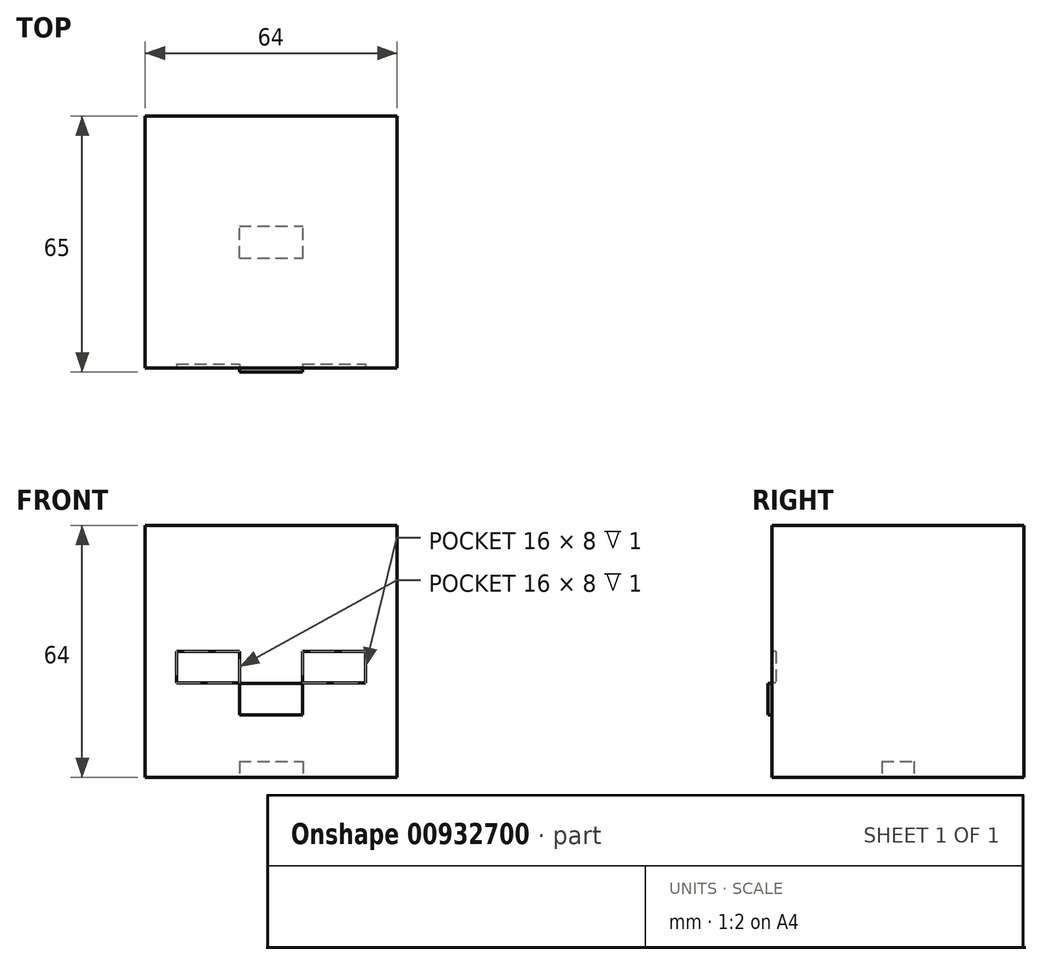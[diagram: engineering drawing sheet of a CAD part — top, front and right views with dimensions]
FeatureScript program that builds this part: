
annotation { "Feature Type Name" : "Feature", "Feature Type Description" : "" }
export const myFeature = defineFeature(function(context is Context, id is Id, definition is map)
    precondition{}
    {
        {
            var Q0;
            Q0=qCreatedBy(makeId("Top.planeOp"),FACE);
            var sketch = newSketch(context, id + "F0", { "sketchPlane" : qUnion([Q0])});
            skLineSegment(sketch, "E0.bottom", {"start": v(-32, 32) * mm, "end": v(32, 32) * mm});
            skLineSegment(sketch, "E0.top", {"start": v(-32, -32) * mm, "end": v(32, -32) * mm});
            skLineSegment(sketch, "E0.left", {"start": v(-32, 32) * mm, "end": v(-32, -32) * mm});
            skLineSegment(sketch, "E0.right", {"start": v(32, 32) * mm, "end": v(32, -32) * mm});
            skSolve(sketch);
        }
        {
            var Q0;
            Q0 = qSketchRegion(id + "F0", true);
            extrude(context, id + "F1", {"entities" : qUnion([Q0]), "depth" : 64 * mm, "offsetDistance" : 25 * mm});
        }
        {
            var Q0;
            Q0=makeQuery(id+"F1.opExtrude","SWEPT_FACE",FACE,{"disambiguationData":[OSD([sQuery(id+"F0.wireOp",EDGE,"E0.top")])]});
            var sketch = newSketch(context, id + "F2", { "sketchPlane" : qUnion([Q0])});
            skLineSegment(sketch, "E1.bottom", {"start": v(-24, 32) * mm, "end": v(-8, 32) * mm});
            skLineSegment(sketch, "E1.top", {"start": v(-24, 24) * mm, "end": v(-8, 24) * mm});
            skLineSegment(sketch, "E1.left", {"start": v(-24, 32) * mm, "end": v(-24, 24) * mm});
            skLineSegment(sketch, "E1.right", {"start": v(-8, 32) * mm, "end": v(-8, 24) * mm});
            skLineSegment(sketch, "E2.bottom", {"start": v(8, 32) * mm, "end": v(24, 32) * mm});
            skLineSegment(sketch, "E2.top", {"start": v(8, 24) * mm, "end": v(24, 24) * mm});
            skLineSegment(sketch, "E2.left", {"start": v(8, 32) * mm, "end": v(8, 24) * mm});
            skLineSegment(sketch, "E2.right", {"start": v(24, 32) * mm, "end": v(24, 24) * mm});
            skLineSegment(sketch, "E3", {"start": v(-32, 32) * mm, "end": v(32, 32) * mm, "construction": true});
            skLineSegment(sketch, "E4.bottom", {"start": v(8, 23.9) * mm, "end": v(-8, 23.9) * mm});
            skLineSegment(sketch, "E4.top", {"start": v(8, 15.9) * mm, "end": v(-8, 15.9) * mm});
            skLineSegment(sketch, "E4.left", {"start": v(8, 23.9) * mm, "end": v(8, 15.9) * mm});
            skLineSegment(sketch, "E4.right", {"start": v(-8, 23.9) * mm, "end": v(-8, 15.9) * mm});
            skSolve(sketch);
        }
        {
            var Q0;
            Q0=makeQuery(id+"F2.imprint","IMPRINT",FACE,{"disambiguationData":[TD([[makeQuery(id+"F2.imprint","IMPRINT",EDGE,{"derivedFrom":sQuery(id+"F2.wireOp",EDGE,"E4.bottom")}),1.0]])]});
            extrude(context, id + "F3", {"entities" : qUnion([Q0]), "operationType" : NewBodyOperationType.ADD, "depth" : 1 * mm, "offsetDistance" : 25 * mm});
        }
        {
            var Q0;
            Q0=makeQuery(id+"F2.imprint","IMPRINT",FACE,{"disambiguationData":[TD([[makeQuery(id+"F2.imprint","IMPRINT",EDGE,{"derivedFrom":sQuery(id+"F2.wireOp",EDGE,"E1.bottom")}),-1.0]])]});
            var Q1;
            Q1=makeQuery(id+"F2.imprint","IMPRINT",FACE,{"disambiguationData":[TD([[makeQuery(id+"F2.imprint","IMPRINT",EDGE,{"derivedFrom":sQuery(id+"F2.wireOp",EDGE,"E2.bottom")}),-1.0]])]});
            extrude(context, id + "F4", {"entities" : qUnion([Q0, Q1]), "operationType" : NewBodyOperationType.REMOVE, "oppositeDirection" : true, "depth" : 1 * mm, "offsetDistance" : 25 * mm});
        }
        {
            var Q0;
            Q0=makeQuery(id+"F1.opExtrude","CAP_FACE",FACE,{"disambiguationData":[OSD([sQuery(id+"F0.wireOp",EDGE,"E0.bottom"),sQuery(id+"F0.wireOp",EDGE,"E0.top"),sQuery(id+"F0.wireOp",EDGE,"E0.left"),sQuery(id+"F0.wireOp",EDGE,"E0.right")])],"isStart":true});
            var sketch = newSketch(context, id + "F5", { "sketchPlane" : qUnion([Q0])});
            skLineSegment(sketch, "E5.bottom", {"start": v(-8.05, 4.05) * mm, "end": v(8.05, 4.05) * mm});
            skLineSegment(sketch, "E5.top", {"start": v(-8.05, -4.05) * mm, "end": v(8.05, -4.05) * mm});
            skLineSegment(sketch, "E5.left", {"start": v(-8.05, 4.05) * mm, "end": v(-8.05, -4.05) * mm});
            skLineSegment(sketch, "E5.right", {"start": v(8.05, 4.05) * mm, "end": v(8.05, -4.05) * mm});
            skSolve(sketch);
        }
        {
            var Q0;
            Q0 = qSketchRegion(id + "F5", true);
            extrude(context, id + "F6", {"entities" : qUnion([Q0]), "operationType" : NewBodyOperationType.REMOVE, "oppositeDirection" : true, "depth" : 4 * mm, "offsetDistance" : 25 * mm});
        }
    });
